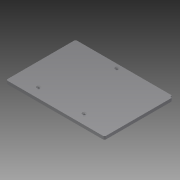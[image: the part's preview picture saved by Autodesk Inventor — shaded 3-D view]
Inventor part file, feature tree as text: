
AUTODESK INVENTOR PART (.ipt)
format: ipt  version: 2013 (Build 170138000, 138)  size: 119,808 bytes
history: native  units: mm
features: sketch x2, extrude x1, hole x1
ambient origin geometry x8: Origin, YZ Plane, XZ Plane, XY Plane, X Axis, Y Axis, Z Axis, Center Point
bodies: Solid1 (feature_tree)
feature tree (4):
  extrude  "Extrusion1"  Depth=119.0mm
  hole  "Hole1"  [1 undecoded]
  sketch  "Sketch1"  dims[d0=8.0mm d1=0.0mm d2=119.0mm]
  sketch  "Sketch3"  dims[d4=145.0mm d5=59.500002mm d6=79.0mm d7=26.5mm d8=10.0mm d9=59.0mm d10=5.0mm d11=5.0mm d12=5.0mm d13=4.0mm d14=2.0mm d15=2.0mm d16=4.0mm d17=4.0mm d18=5.0mm d19=5.0mm d20=10.0mm d21=6.0mm d22=4.0mm d23=2.0mm d24=90.0deg d25=1e-05mm d26=15.882496mm]
note: 1 required parameter value undecoded (feature->parameter linkage not recoverable at this tier; creation-order binding heuristic only, values carry confidence <= 0.55)
